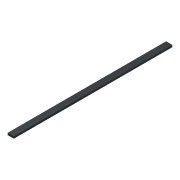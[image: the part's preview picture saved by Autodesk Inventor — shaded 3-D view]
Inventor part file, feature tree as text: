
AUTODESK INVENTOR PART (.ipt)
format: ipt  version: 2018 (Build 220112000, 112)  size: 88,576 bytes
history: native  units: mm
features: sketch x2, extrude x1, hole x1
ambient origin geometry x8: Origin, YZ Plane, XZ Plane, XY Plane, X Axis, Y Axis, Z Axis, Center Point
bodies: Solid1 (feature_tree)
feature tree (4):
  extrude  "Extrusion1"  Depth=798.434mm
  hole  "Hole2"  [1 undecoded]
  sketch  "Sketch1"  dims[d0=30.0mm d1=798.434mm]
  sketch  "Sketch5"  dims[d2=10.0mm d3=0.0mm d25=50.0mm d26=100.0mm d27=15.0mm d28=15.0mm d29=3.0mm d30=6.0mm d31=6.1mm d32=2.0mm d33=90.0deg d34=8.0mm d35=20.594885mm]
note: 1 required parameter value undecoded (feature->parameter linkage not recoverable at this tier; creation-order binding heuristic only, values carry confidence <= 0.55)
